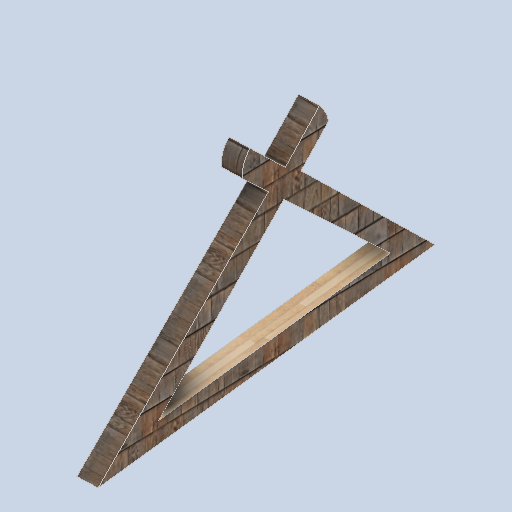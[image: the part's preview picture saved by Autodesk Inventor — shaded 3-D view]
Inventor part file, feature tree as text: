
AUTODESK INVENTOR PART (.ipt)
format: ipt  version: 2024.2 (Build 282272000, 272)  size: 233,984 bytes
history: native  units: in
note: dims shown in document units (in); Inventor stores cm internally (conversion verified against a paired STEP export)
features: sketch x10, plane x8, other x3
ambient origin geometry x8: Origin, YZ Plane, XZ Plane, XY Plane, X Axis, Y Axis, Z Axis, Center Point
bodies: Solid1 (feature_tree)
feature tree (21):
  other  "pad_outframe_02_MIR.ipt"
  other  "Solid1::pad_outframe_02_MIR.ipt"
  other  "TaggingFeature1"
  sketch  "Sketch1"  dims[d0=0.3937in]
  sketch  "Sketch2"
  sketch  "Sketch3"
  sketch  "Sketch6"
  sketch  "Sketch7"
  sketch  "Sketch8"
  sketch  "Sketch9"
  sketch  "Sketch10"
  sketch  "Sketch11"
  sketch  "Sketch12"
  plane  "Work Plane1"
  plane  "Work Plane2"
  plane  "Work Plane3"
  plane  "Work Plane4"
  plane  "Work Plane5"
  plane  "Work Plane6"
  plane  "Work Plane7"
  plane  "Work Plane8"
